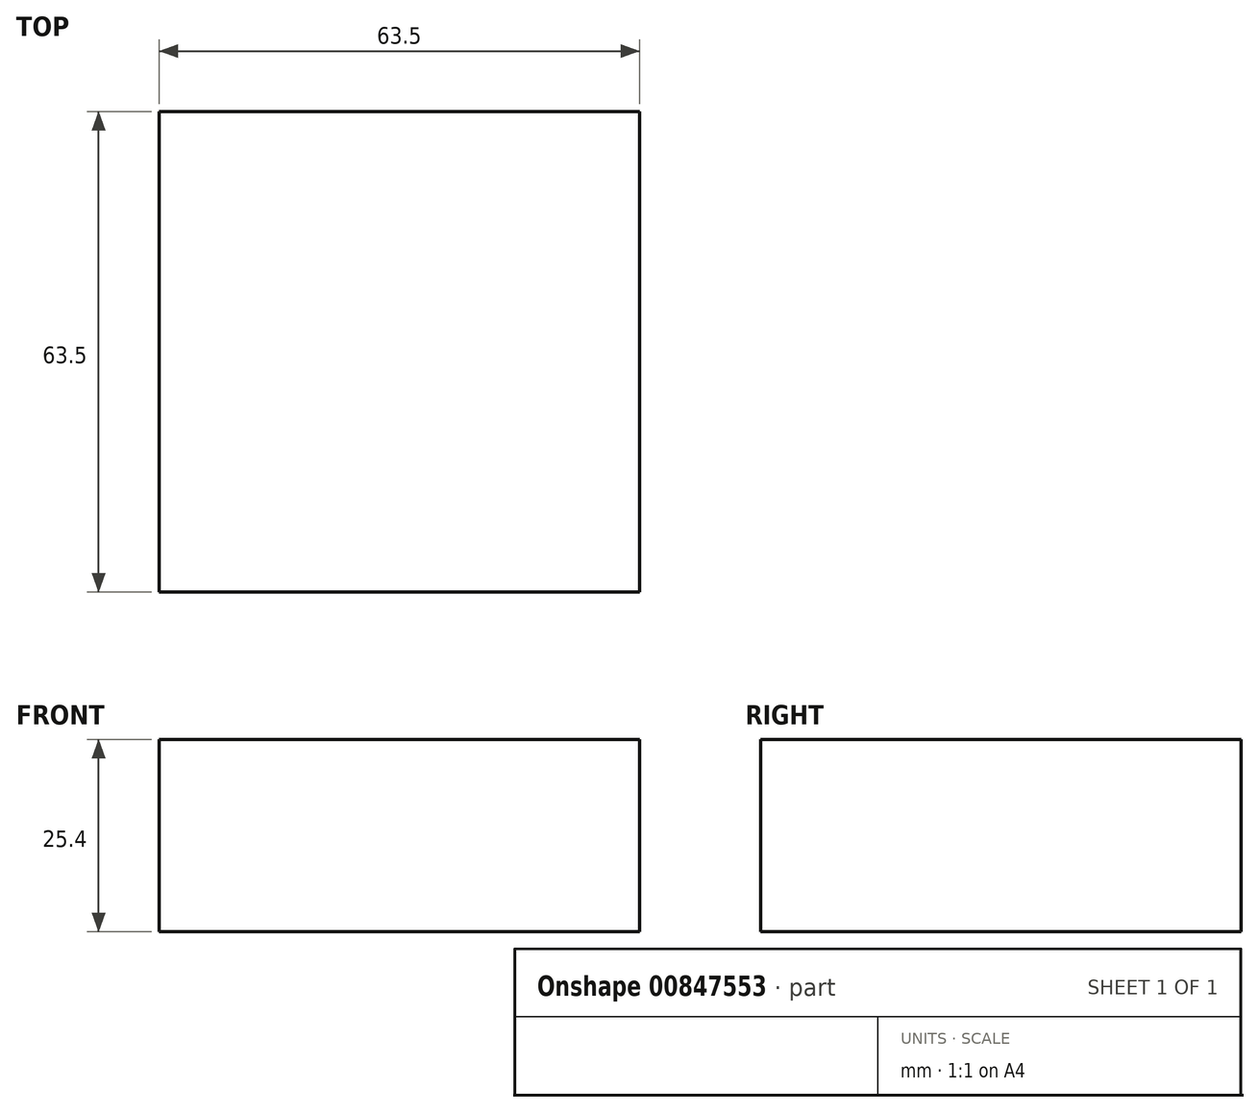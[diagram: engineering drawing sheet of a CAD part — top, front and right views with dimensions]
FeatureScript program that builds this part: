
annotation { "Feature Type Name" : "Feature", "Feature Type Description" : "" }
export const myFeature = defineFeature(function(context is Context, id is Id, definition is map)
    precondition{}
    {
        {
            var Q0;
            Q0=qCreatedBy(makeId("Top.planeOp"),FACE);
            var sketch = newSketch(context, id + "F0", { "sketchPlane" : qUnion([Q0])});
            skLineSegment(sketch, "E0.bottom", {"start": v(-27.8, 32.03) * mm, "end": v(35.7, 32.03) * mm});
            skLineSegment(sketch, "E0.top", {"start": v(-27.8, -31.47) * mm, "end": v(35.7, -31.47) * mm});
            skLineSegment(sketch, "E0.left", {"start": v(-27.8, 32.03) * mm, "end": v(-27.8, -31.47) * mm});
            skLineSegment(sketch, "E0.right", {"start": v(35.7, 32.03) * mm, "end": v(35.7, -31.47) * mm});
            skSolve(sketch);
        }
        {
            var Q0;
            Q0=makeQuery(id+"F0.imprint","IMPRINT",FACE,{"disambiguationData":[TD([[makeQuery(id+"F0.imprint","IMPRINT",EDGE,{"derivedFrom":sQuery(id+"F0.wireOp",EDGE,"E0.bottom")}),-1.0]])]});
            extrude(context, id + "F1", {"entities" : qUnion([Q0]), "depth" : 25.4 * mm, "offsetDistance" : 25.4 * mm});
        }
    });
